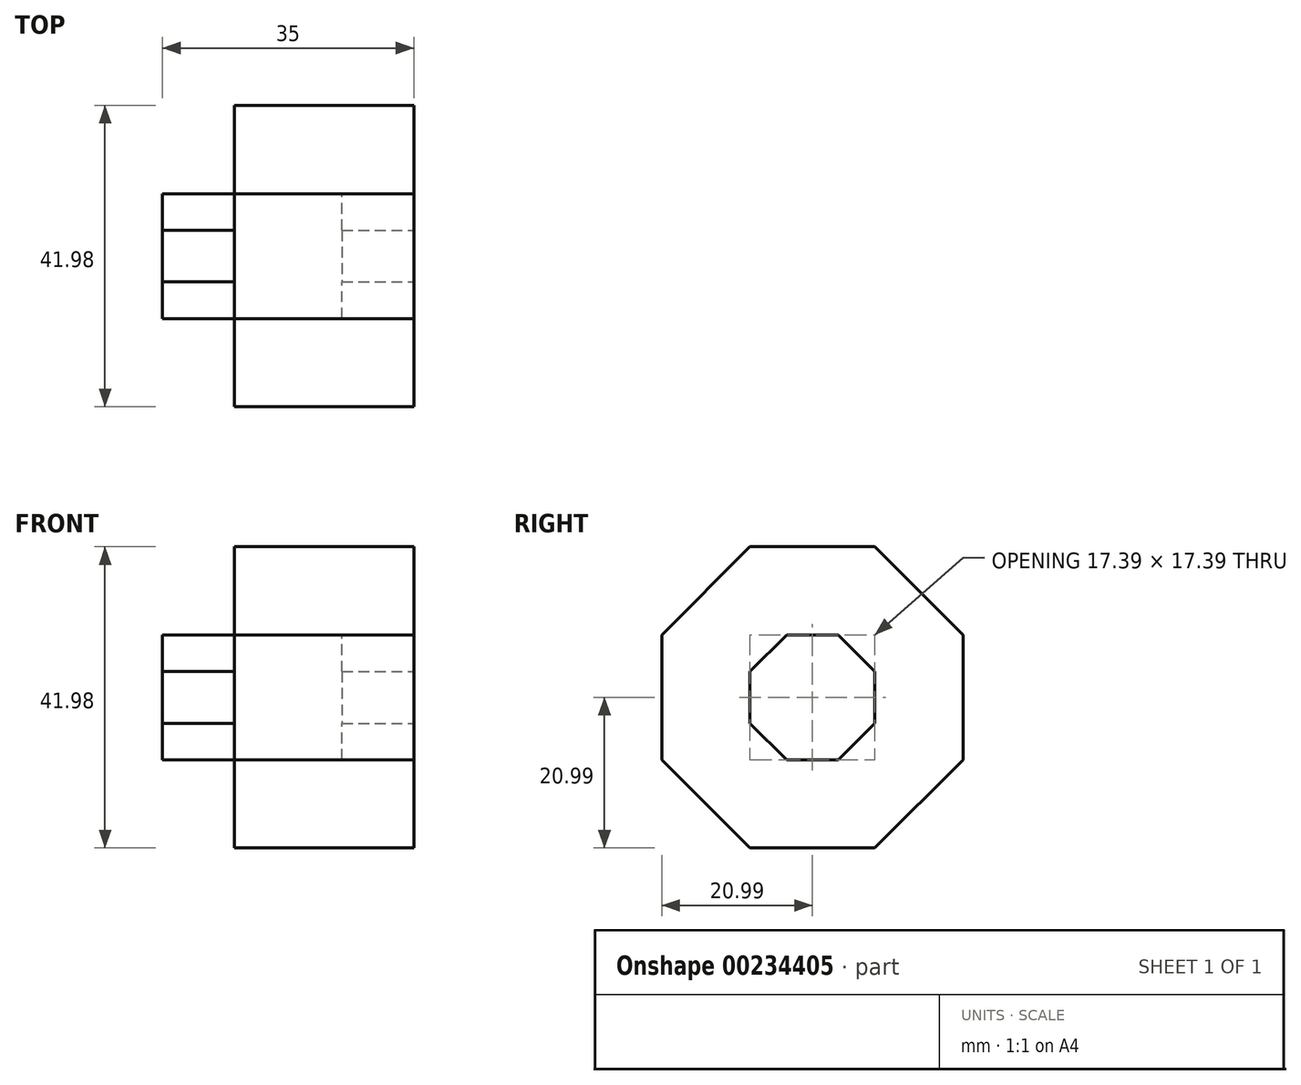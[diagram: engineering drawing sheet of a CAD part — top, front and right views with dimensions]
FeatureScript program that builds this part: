
annotation { "Feature Type Name" : "Feature", "Feature Type Description" : "" }
export const myFeature = defineFeature(function(context is Context, id is Id, definition is map)
    precondition{}
    {
        {
            var Q0;
            Q0=qCreatedBy(makeId("Right.planeOp"),FACE);
            var sketch = newSketch(context, id + "F0", { "sketchPlane" : qUnion([Q0])});
            skLineSegment(sketch, "E0.0", {"start": v(21, -8.7) * mm, "end": v(8.7, -21) * mm});
            skLineSegment(sketch, "E0.1", {"start": v(8.7, -21) * mm, "end": v(-8.7, -21) * mm});
            skLineSegment(sketch, "E0.2", {"start": v(-8.7, -21) * mm, "end": v(-21, -8.7) * mm});
            skLineSegment(sketch, "E0.3", {"start": v(-21, -8.7) * mm, "end": v(-21, 8.7) * mm});
            skLineSegment(sketch, "E0.4", {"start": v(-21, 8.7) * mm, "end": v(-8.7, 21) * mm});
            skLineSegment(sketch, "E0.5", {"start": v(-8.7, 21) * mm, "end": v(8.7, 21) * mm});
            skLineSegment(sketch, "E0.6", {"start": v(8.7, 21) * mm, "end": v(21, 8.7) * mm});
            skLineSegment(sketch, "E0.7", {"start": v(21, 8.7) * mm, "end": v(21, -8.7) * mm});
            skPoint(sketch, "E0.0.midPoint", {"position": v(14.84, -14.84) * mm});
            skSolve(sketch);
        }
        {
            var Q0;
            Q0=makeQuery(id+"F0.imprint","IMPRINT",FACE,{"disambiguationData":[TD([[makeQuery(id+"F0.imprint","IMPRINT",EDGE,{"derivedFrom":sQuery(id+"F0.wireOp",EDGE,"E0.0")}),-1.0]])]});
            extrude(context, id + "F1", {"entities" : qUnion([Q0]), "depth" : 25 * mm});
        }
        {
            var Q0;
            Q0=makeQuery(id+"F1.opExtrude","CAP_FACE",FACE,{"disambiguationData":[OSD([sQuery(id+"F0.wireOp",EDGE,"E0.0"),sQuery(id+"F0.wireOp",EDGE,"E0.1"),sQuery(id+"F0.wireOp",EDGE,"E0.2"),sQuery(id+"F0.wireOp",EDGE,"E0.3"),sQuery(id+"F0.wireOp",EDGE,"E0.4"),sQuery(id+"F0.wireOp",EDGE,"E0.5"),sQuery(id+"F0.wireOp",EDGE,"E0.6"),sQuery(id+"F0.wireOp",EDGE,"E0.7")])],"isStart":true});
            var sketch = newSketch(context, id + "F2", { "sketchPlane" : qUnion([Q0])});
            skLineSegment(sketch, "E1", {"start": v(-8.7, 21) * mm, "end": v(-8.7, -21) * mm});
            skLineSegment(sketch, "E2", {"start": v(8.7, 21) * mm, "end": v(8.7, -21) * mm});
            skLineSegment(sketch, "E3", {"start": v(-21, 8.7) * mm, "end": v(21, 8.7) * mm});
            skLineSegment(sketch, "E4", {"start": v(-21, -8.7) * mm, "end": v(21, -8.7) * mm});
            skLineSegment(sketch, "E5", {"start": v(-3.6, 8.7) * mm, "end": v(-8.7, 3.6) * mm});
            skLineSegment(sketch, "E6", {"start": v(8.7, -3.6) * mm, "end": v(3.6, -8.7) * mm});
            skLineSegment(sketch, "E7", {"start": v(-8.7, -3.6) * mm, "end": v(-3.6, -8.7) * mm});
            skLineSegment(sketch, "E8", {"start": v(3.6, 8.7) * mm, "end": v(8.7, 3.6) * mm});
            skSolve(sketch);
        }
        {
            var Q0;
            {var subQ3=sQuery(id+"F2.wireOp",EDGE,"E5");Q0=makeQuery(id+"F2.imprint","IMPRINT",FACE,{"disambiguationData":[TD([[makeQuery(id+"F2.imprint","IMPRINT",EDGE,{"derivedFrom":subQ3}),1.0]])]});}
            extrude(context, id + "F3", {"entities" : qUnion([Q0]), "operationType" : NewBodyOperationType.ADD, "depth" : 10 * mm});
        }
        {
            var Q0;
            Q0=makeQuery(id+"F1.opExtrude","CAP_FACE",FACE,{"disambiguationData":[OSD([sQuery(id+"F0.wireOp",EDGE,"E0.0"),sQuery(id+"F0.wireOp",EDGE,"E0.1"),sQuery(id+"F0.wireOp",EDGE,"E0.2"),sQuery(id+"F0.wireOp",EDGE,"E0.3"),sQuery(id+"F0.wireOp",EDGE,"E0.4"),sQuery(id+"F0.wireOp",EDGE,"E0.5"),sQuery(id+"F0.wireOp",EDGE,"E0.6"),sQuery(id+"F0.wireOp",EDGE,"E0.7")])],"isStart":false});
            var sketch = newSketch(context, id + "F4", { "sketchPlane" : qUnion([Q0])});
            skLineSegment(sketch, "E9", {"start": v(-8.7, 3.6) * mm, "end": v(-8.7, -3.6) * mm});
            skLineSegment(sketch, "E10", {"start": v(8.7, 3.6) * mm, "end": v(8.7, -3.6) * mm});
            skLineSegment(sketch, "E11", {"start": v(-3.6, 8.7) * mm, "end": v(3.6, 8.7) * mm});
            skLineSegment(sketch, "E12", {"start": v(-21, -8.7) * mm, "end": v(8.7, 21) * mm});
            skLineSegment(sketch, "E13", {"start": v(8.7, 21) * mm, "end": v(21, 8.7) * mm});
            skLineSegment(sketch, "E14", {"start": v(-8.7, -21) * mm, "end": v(21, 8.7) * mm});
            skLineSegment(sketch, "E15", {"start": v(-8.7, 21) * mm, "end": v(21, -8.7) * mm});
            skLineSegment(sketch, "E16", {"start": v(8.7, -21) * mm, "end": v(-21, 8.7) * mm});
            skLineSegment(sketch, "E17.trimOffspring", {"start": v(3.6, -8.7) * mm, "end": v(-3.6, -8.7) * mm});
            skSolve(sketch);
        }
        {
            var Q0;
            {var subQ1=sQuery(id+"F4.wireOp",EDGE,"E9");Q0=makeQuery(id+"F4.imprint","IMPRINT",FACE,{"disambiguationData":[TD([[makeQuery(id+"F4.imprint","IMPRINT",EDGE,{"derivedFrom":subQ1}),1.0]])]});}
            extrude(context, id + "F5", {"entities" : qUnion([Q0]), "operationType" : NewBodyOperationType.REMOVE, "oppositeDirection" : true, "depth" : 10 * mm});
        }
    });
